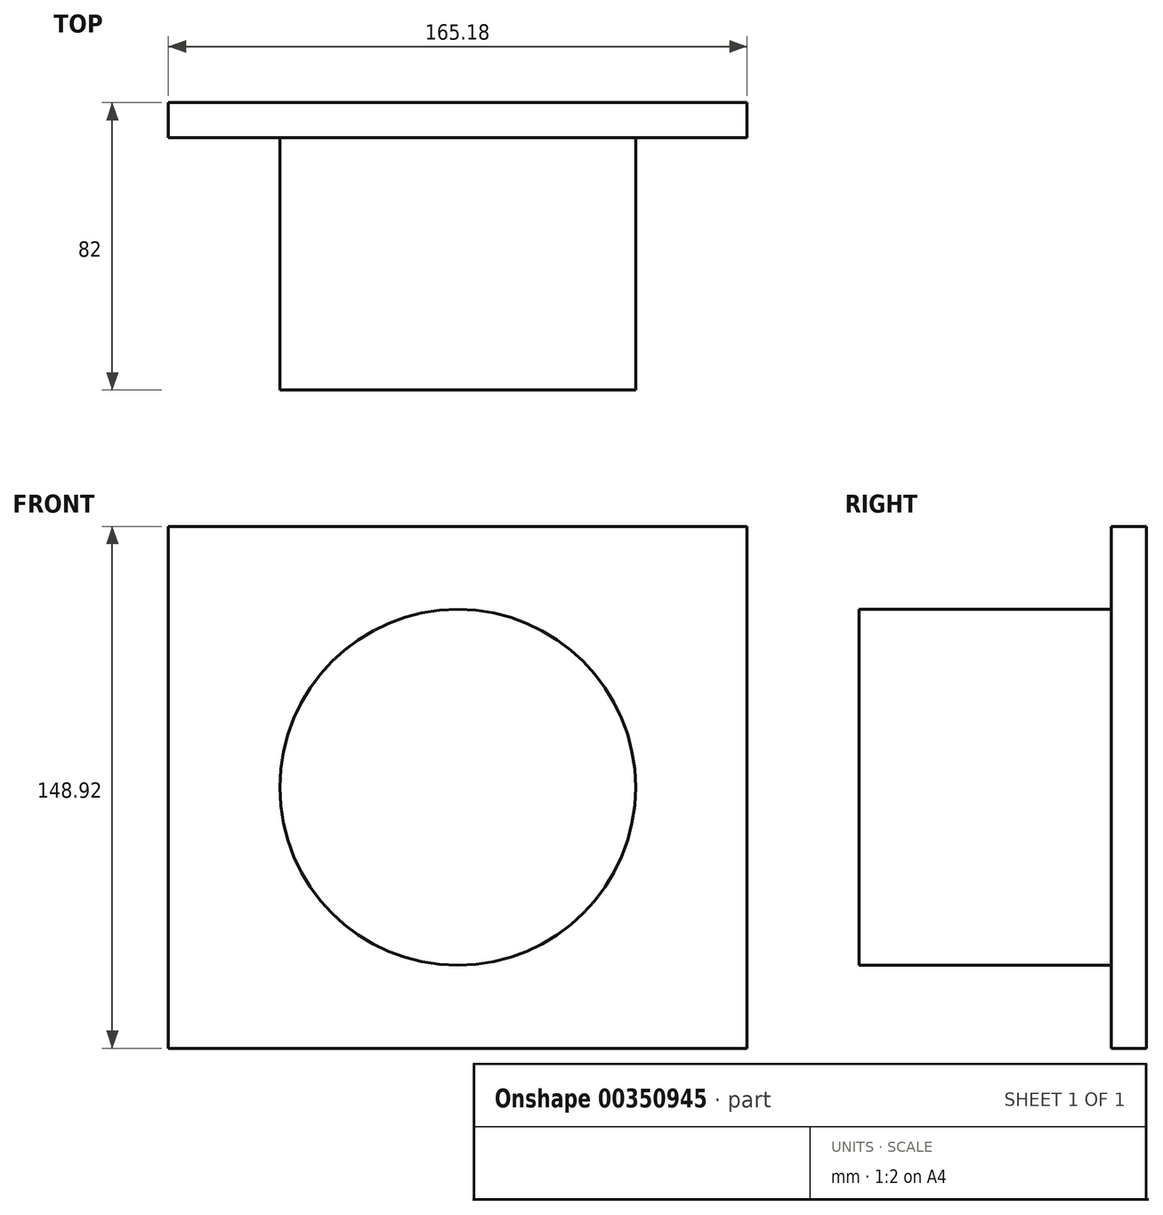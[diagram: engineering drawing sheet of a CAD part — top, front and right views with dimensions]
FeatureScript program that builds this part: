
annotation { "Feature Type Name" : "Feature", "Feature Type Description" : "" }
export const myFeature = defineFeature(function(context is Context, id is Id, definition is map)
    precondition{}
    {
        {
            var Q0;
            Q0=qCreatedBy(makeId("Front.planeOp"),FACE);
            var sketch = newSketch(context, id + "F0", { "sketchPlane" : qUnion([Q0])});
            skLineSegment(sketch, "E0.bottom", {"start": v(-82.6, 74.46) * mm, "end": v(82.6, 74.46) * mm});
            skLineSegment(sketch, "E0.top", {"start": v(-82.6, -74.46) * mm, "end": v(82.6, -74.46) * mm});
            skLineSegment(sketch, "E0.left", {"start": v(-82.6, 74.46) * mm, "end": v(-82.6, -74.46) * mm});
            skLineSegment(sketch, "E0.right", {"start": v(82.6, 74.46) * mm, "end": v(82.6, -74.46) * mm});
            skPoint(sketch, "E0.middle", {"position": v(0, 0) * mm});
            skCircle(sketch, "E1", {"center": v(0, 0) * mm, "radius": 50.8 * mm});
            skSolve(sketch);
        }
        {
            var Q0;
            Q0 = qSketchRegion(id + "F0", true);
            var Q1;
            Q1=makeQuery(id+"F0.imprint","IMPRINT",FACE,{"disambiguationData":[TD([[makeQuery(id+"F0.imprint","IMPRINT",EDGE,{"derivedFrom":sQuery(id+"F0.wireOp",EDGE,"E1")}),1.0]])]});
            extrude(context, id + "F1", {"entities" : qUnion([Q0, Q1]), "depth" : 3 * mm});
        }
        {
            var Q0;
            Q0=makeQuery(id+"F0.imprint","IMPRINT",FACE,{"disambiguationData":[TD([[makeQuery(id+"F0.imprint","IMPRINT",EDGE,{"derivedFrom":sQuery(id+"F0.wireOp",EDGE,"E1")}),1.0]])]});
            extrude(context, id + "F2", {"entities" : qUnion([Q0]), "operationType" : NewBodyOperationType.ADD, "depth" : 75 * mm});
        }
        {
            var Q0;
            Q0=makeQuery(id+"F1.opExtrude","CAP_FACE",FACE,{"disambiguationData":[OSD([sQuery(id+"F0.wireOp",EDGE,"E0.bottom"),sQuery(id+"F0.wireOp",EDGE,"E0.top"),sQuery(id+"F0.wireOp",EDGE,"E0.left"),sQuery(id+"F0.wireOp",EDGE,"E0.right")])],"isStart":true});
            extrude(context, id + "F3", {"entities" : qUnion([Q0]), "operationType" : NewBodyOperationType.ADD, "depth" : 7 * mm});
        }
    });
